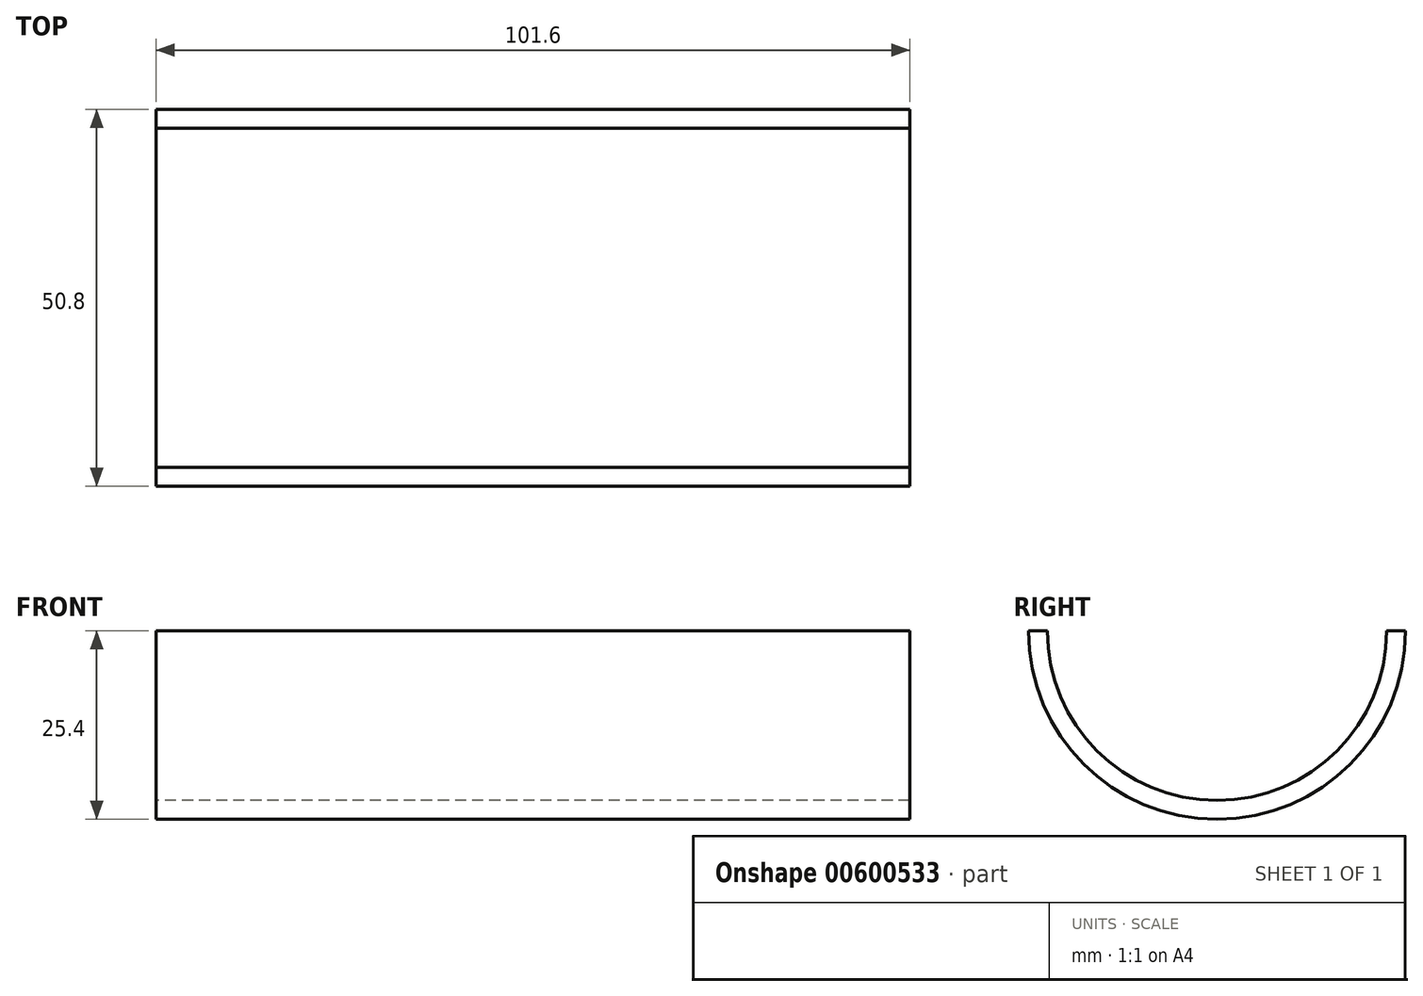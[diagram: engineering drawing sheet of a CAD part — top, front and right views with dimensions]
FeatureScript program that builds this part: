
annotation { "Feature Type Name" : "Feature", "Feature Type Description" : "" }
export const myFeature = defineFeature(function(context is Context, id is Id, definition is map)
    precondition{}
    {
        {
            var Q0;
            Q0=qCreatedBy(makeId("Right.planeOp"),FACE);
            var sketch = newSketch(context, id + "F0", { "sketchPlane" : qUnion([Q0])});
            skArc(sketch, "E0", {"start": v(-25.4, 0) * mm, "mid": v(0, -25.4) * mm, "end": v(25.4, 0) * mm});
            skLineSegment(sketch, "E1", {"start": v(-25.4, 0) * mm, "end": v(-22.86, 0) * mm});
            skArc(sketch, "E2.0", {"start": v(-22.86, 0) * mm, "mid": v(0, -22.86) * mm, "end": v(22.86, 0) * mm});
            skLineSegment(sketch, "E3.trimOffspring", {"start": v(22.86, 0) * mm, "end": v(25.4, 0) * mm});
            skSolve(sketch);
        }
        {
            var Q0;
            Q0 = qSketchRegion(id + "F0", true);
            extrude(context, id + "F1", {"entities" : qUnion([Q0]), "depth" : 50.8 * mm, "offsetDistance" : 25.4 * mm, "hasSecondDirection" : true, "secondDirectionOppositeDirection" : true, "secondDirectionDepth" : 50.8 * mm});
        }
    });
